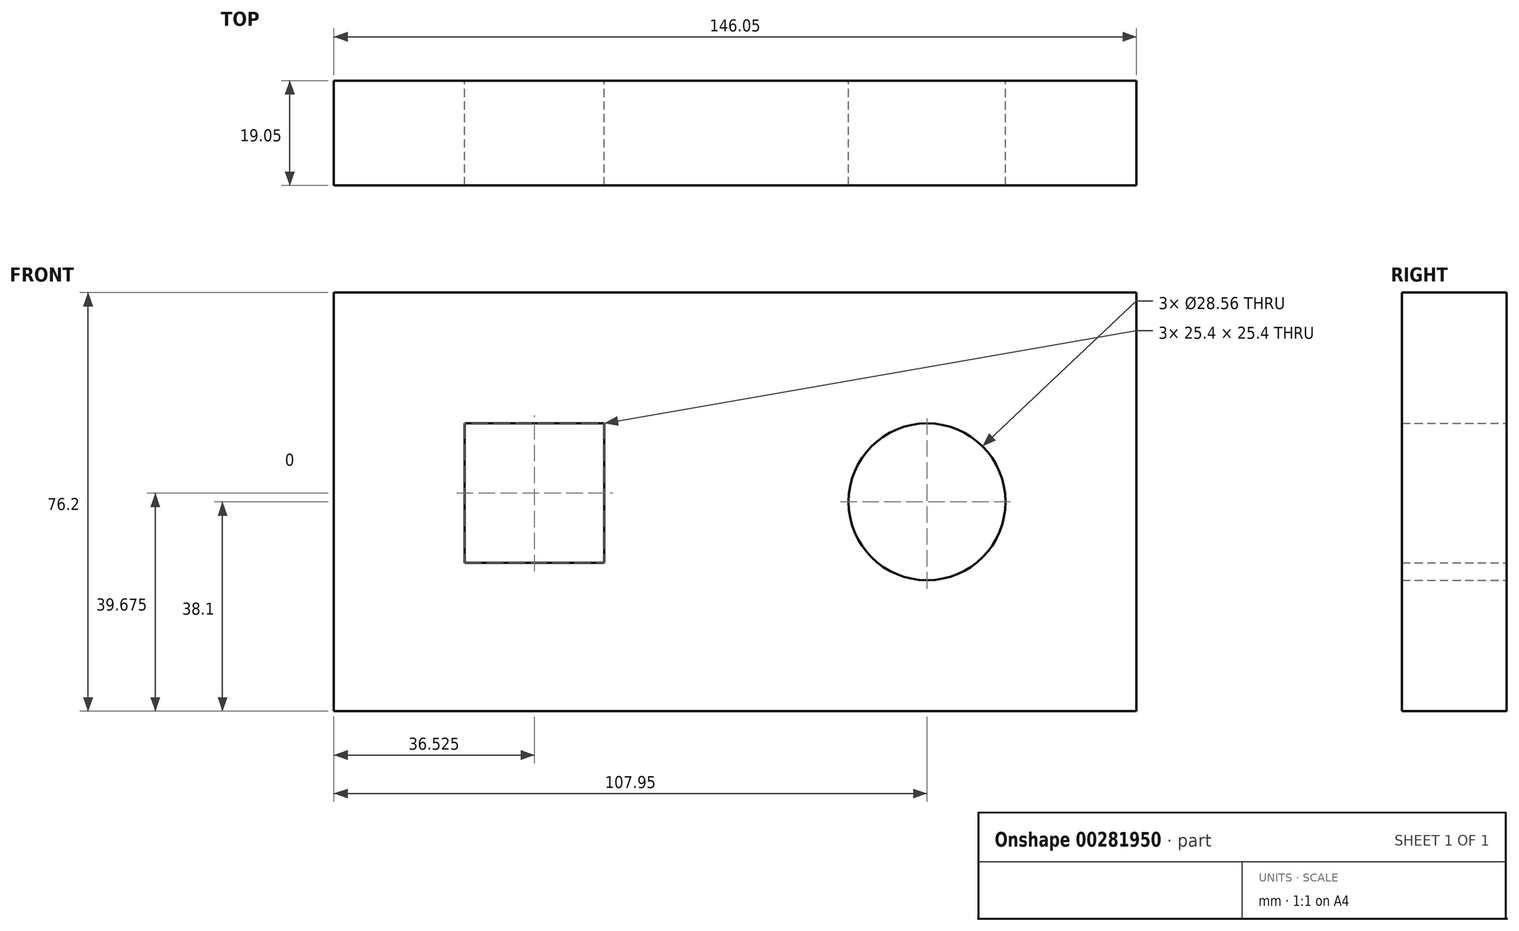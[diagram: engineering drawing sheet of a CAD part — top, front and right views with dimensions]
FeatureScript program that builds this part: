
annotation { "Feature Type Name" : "Feature", "Feature Type Description" : "" }
export const myFeature = defineFeature(function(context is Context, id is Id, definition is map)
    precondition{}
    {
        {
            var Q0;
            Q0=qCreatedBy(makeId("Front.planeOp"),FACE);
            var sketch = newSketch(context, id + "F0", { "sketchPlane" : qUnion([Q0])});
            skLineSegment(sketch, "E0.bottom", {"start": v(0, 0) * mm, "end": v(-146.05, 0) * mm});
            skLineSegment(sketch, "E0.top", {"start": v(0, 76.2) * mm, "end": v(-146.05, 76.2) * mm});
            skLineSegment(sketch, "E0.left", {"start": v(0, 0) * mm, "end": v(0, 76.2) * mm});
            skLineSegment(sketch, "E0.right", {"start": v(-146.05, 0) * mm, "end": v(-146.05, 76.2) * mm});
            skLineSegment(sketch, "E1.bottom", {"start": v(-122.22, 52.37) * mm, "end": v(-96.82, 52.37) * mm});
            skLineSegment(sketch, "E1.top", {"start": v(-122.22, 26.97) * mm, "end": v(-96.82, 26.97) * mm});
            skLineSegment(sketch, "E1.left", {"start": v(-122.22, 52.37) * mm, "end": v(-122.22, 26.97) * mm});
            skLineSegment(sketch, "E1.right", {"start": v(-96.82, 52.37) * mm, "end": v(-96.82, 26.97) * mm});
            skCircle(sketch, "E2", {"center": v(-38.1, 38.1) * mm, "radius": 14.28 * mm});
            skSolve(sketch);
        }
        {
            var Q0;
            Q0=makeQuery(id+"F0.imprint","IMPRINT",FACE,{"disambiguationData":[TD([[makeQuery(id+"F0.imprint","IMPRINT",EDGE,{"derivedFrom":sQuery(id+"F0.wireOp",EDGE,"E0.bottom")}),-1.0]])]});
            extrude(context, id + "F1", {"entities" : qUnion([Q0]), "depth" : 19.05 * mm});
        }
    });
